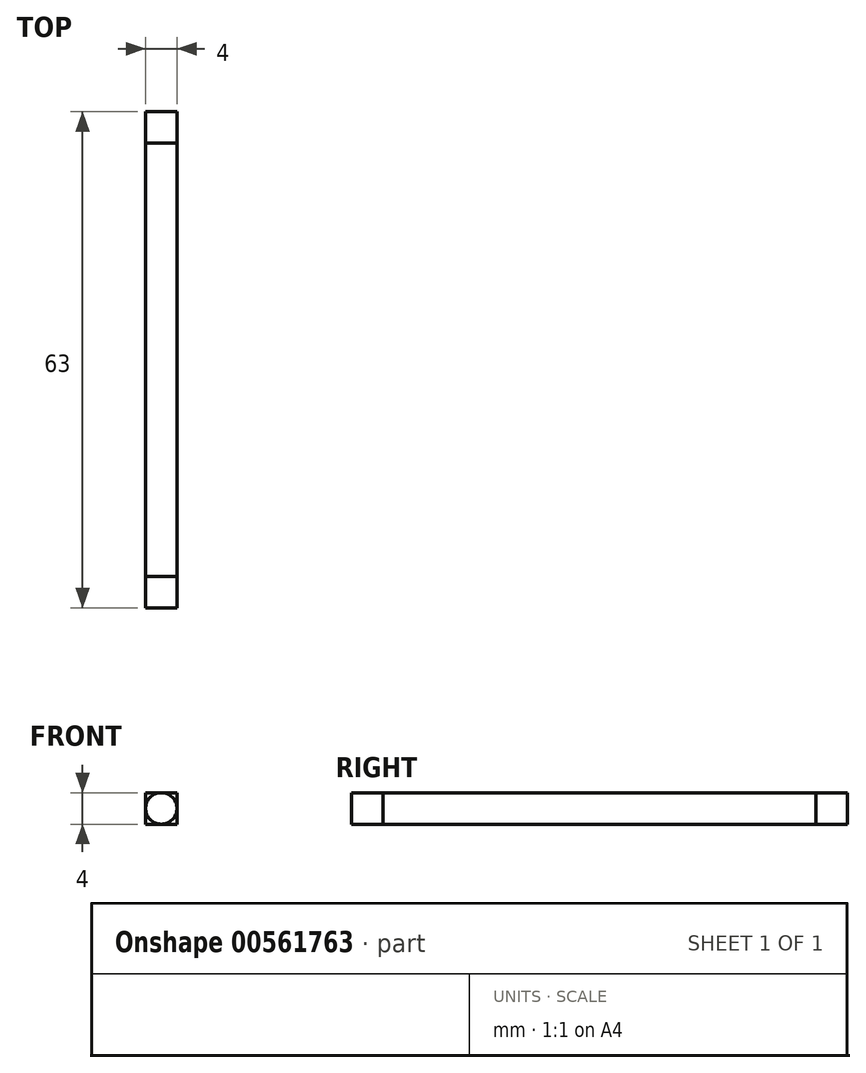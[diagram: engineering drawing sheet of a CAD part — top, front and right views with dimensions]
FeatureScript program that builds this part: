
annotation { "Feature Type Name" : "Feature", "Feature Type Description" : "" }
export const myFeature = defineFeature(function(context is Context, id is Id, definition is map)
    precondition{}
    {
        {
            var Q0;
            Q0=qCreatedBy(makeId("Front.planeOp"),FACE);
            var sketch = newSketch(context, id + "F0", { "sketchPlane" : qUnion([Q0])});
            skLineSegment(sketch, "E0.bottom", {"start": v(-2, 2) * mm, "end": v(2, 2) * mm});
            skLineSegment(sketch, "E0.top", {"start": v(-2, -2) * mm, "end": v(2, -2) * mm});
            skLineSegment(sketch, "E0.left", {"start": v(-2, 2) * mm, "end": v(-2, -2) * mm});
            skLineSegment(sketch, "E0.right", {"start": v(2, 2) * mm, "end": v(2, -2) * mm});
            skPoint(sketch, "E0.middle", {"position": v(0, 0) * mm});
            skSolve(sketch);
        }
        {
            var Q0;
            Q0 = qSketchRegion(id + "F0", true);
            extrude(context, id + "F1", {"entities" : qUnion([Q0]), "depth" : 55 * mm, "offsetDistance" : 25 * mm});
        }
        {
            var Q0;
            Q0=makeQuery(id+"F1.opExtrude","CAP_FACE",FACE,{"disambiguationData":[OSD([sQuery(id+"F0.wireOp",EDGE,"E0.bottom"),sQuery(id+"F0.wireOp",EDGE,"E0.top"),sQuery(id+"F0.wireOp",EDGE,"E0.left"),sQuery(id+"F0.wireOp",EDGE,"E0.right")])],"isStart":false});
            var sketch = newSketch(context, id + "F2", { "sketchPlane" : qUnion([Q0])});
            skCircle(sketch, "E1", {"center": v(0, 0) * mm, "radius": 2 * mm});
            skSolve(sketch);
        }
        {
            var Q0;
            Q0 = qSketchRegion(id + "F2", true);
            extrude(context, id + "F3", {"entities" : qUnion([Q0]), "operationType" : NewBodyOperationType.ADD, "depth" : 4 * mm, "offsetDistance" : 25 * mm});
        }
        {
            var Q0;
            Q0=makeQuery(id+"F1.opExtrude","CAP_FACE",FACE,{"disambiguationData":[OSD([sQuery(id+"F0.wireOp",EDGE,"E0.bottom"),sQuery(id+"F0.wireOp",EDGE,"E0.top"),sQuery(id+"F0.wireOp",EDGE,"E0.left"),sQuery(id+"F0.wireOp",EDGE,"E0.right")])],"isStart":true});
            var sketch = newSketch(context, id + "F4", { "sketchPlane" : qUnion([Q0])});
            skCircle(sketch, "E2", {"center": v(0, 0) * mm, "radius": 2 * mm});
            skSolve(sketch);
        }
        {
            var Q0;
            Q0 = qSketchRegion(id + "F4", true);
            extrude(context, id + "F5", {"entities" : qUnion([Q0]), "operationType" : NewBodyOperationType.ADD, "depth" : 4 * mm, "offsetDistance" : 25 * mm});
        }
    });
